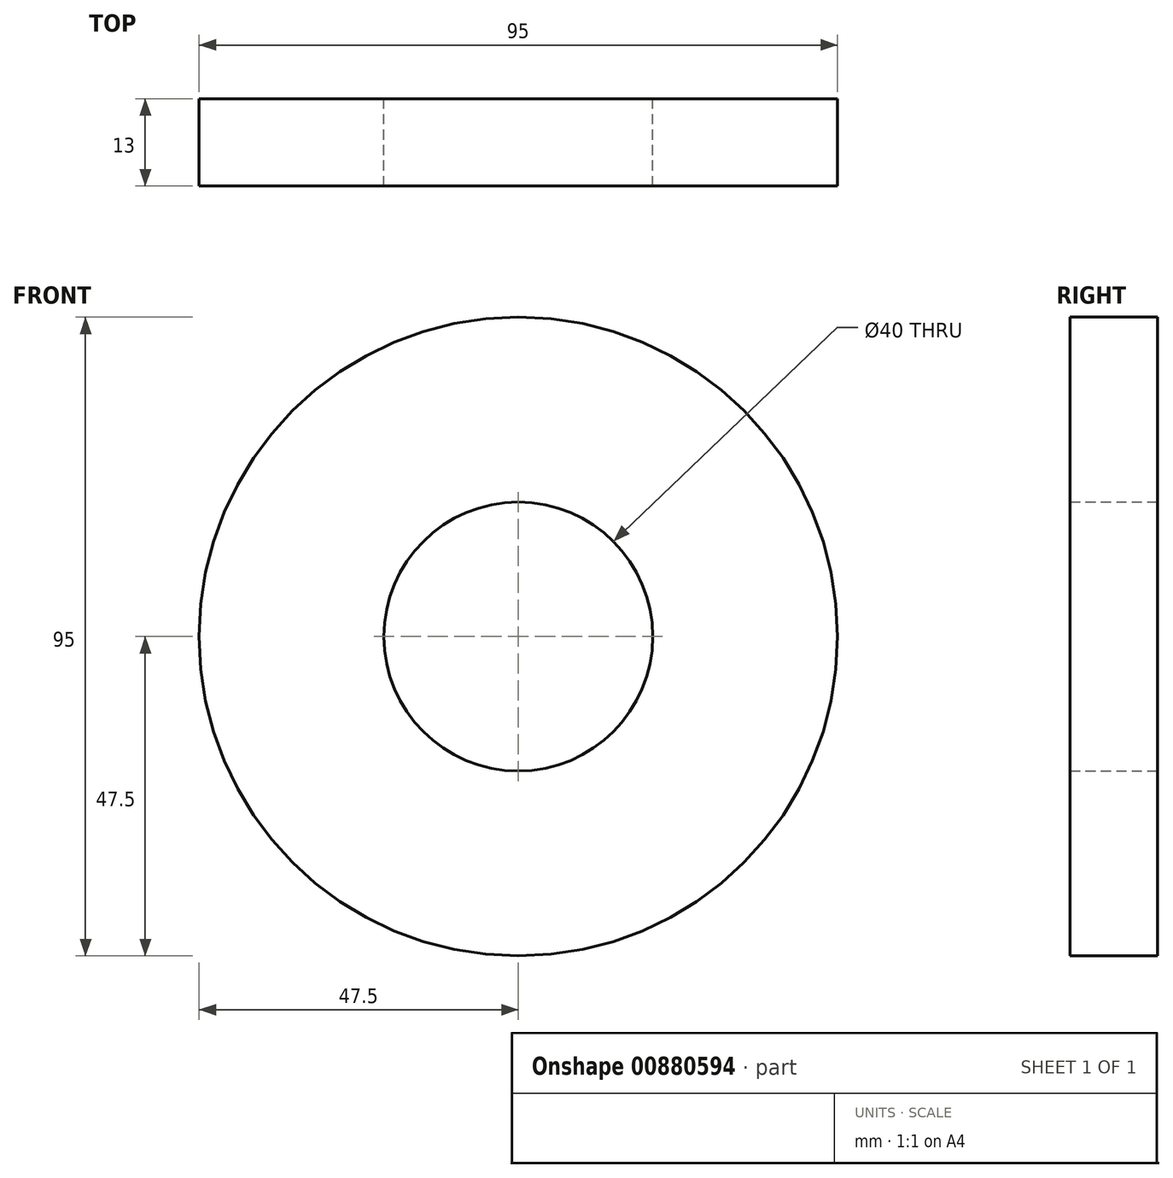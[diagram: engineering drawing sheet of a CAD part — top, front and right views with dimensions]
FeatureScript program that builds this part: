
annotation { "Feature Type Name" : "Feature", "Feature Type Description" : "" }
export const myFeature = defineFeature(function(context is Context, id is Id, definition is map)
    precondition{}
    {
        {
            var Q0;
            Q0=qCreatedBy(makeId("Front.planeOp"),FACE);
            var sketch = newSketch(context, id + "F0", { "sketchPlane" : qUnion([Q0])});
            skCircle(sketch, "E0", {"center": v(0, 0) * mm, "radius": 20 * mm});
            skCircle(sketch, "E1", {"center": v(0, 0) * mm, "radius": 47.5 * mm});
            skSolve(sketch);
        }
        {
            var Q0;
            Q0 = qSketchRegion(id + "F0", true);
            extrude(context, id + "F1", {"entities" : qUnion([Q0]), "depth" : 13 * mm, "offsetDistance" : 25 * mm});
        }
    });
